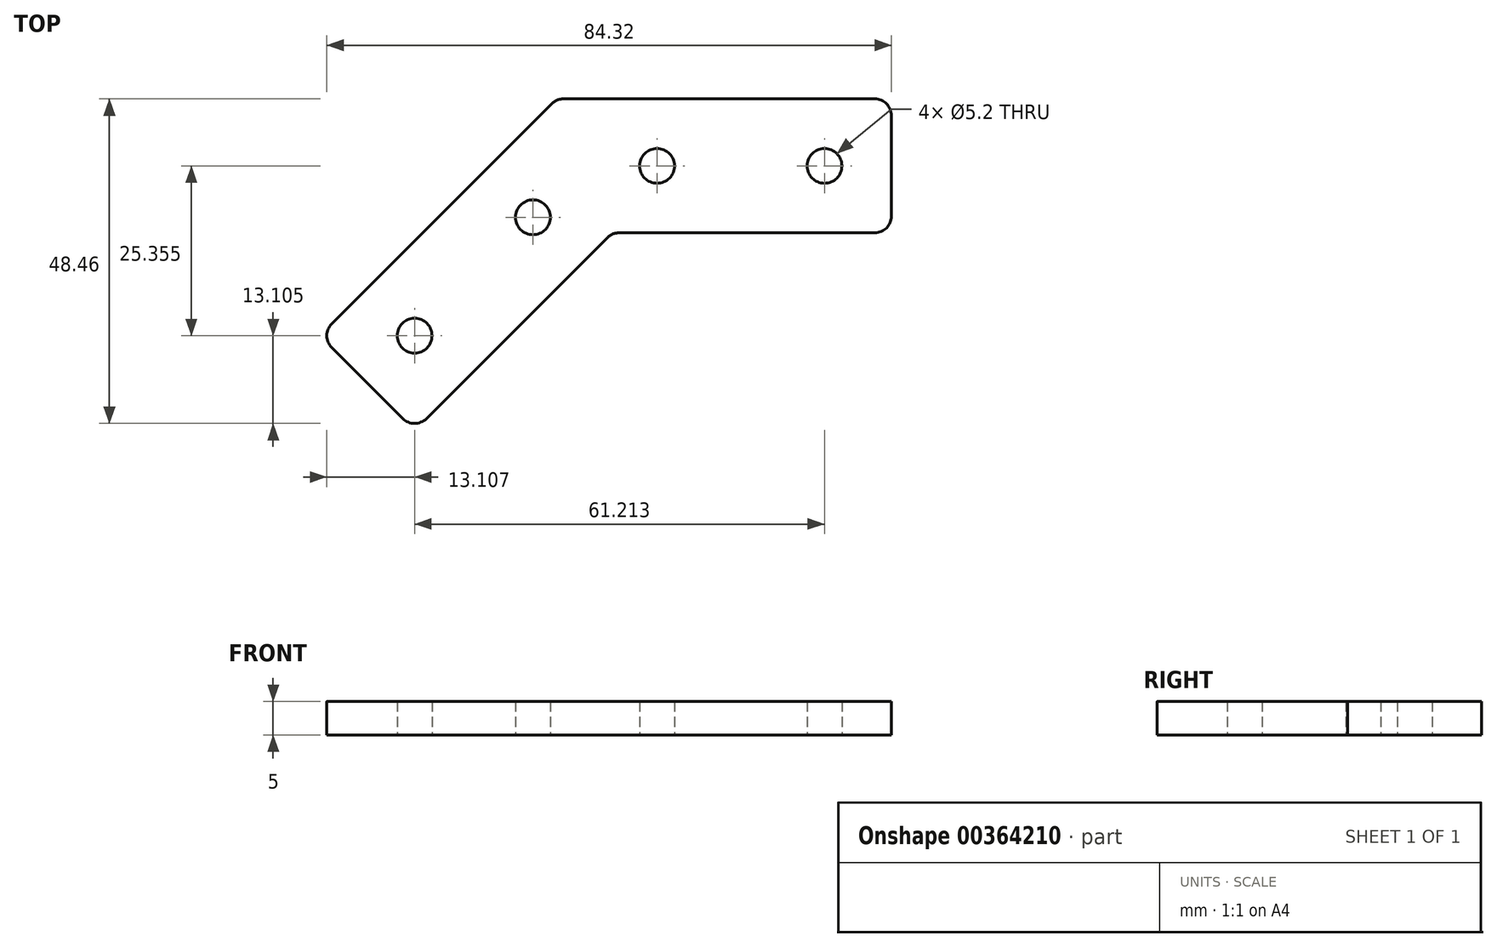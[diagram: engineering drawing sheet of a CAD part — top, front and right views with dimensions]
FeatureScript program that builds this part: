
annotation { "Feature Type Name" : "Feature", "Feature Type Description" : "" }
export const myFeature = defineFeature(function(context is Context, id is Id, definition is map)
    precondition{}
    {
        {
            var Q0;
            Q0=qCreatedBy(makeId("Top.planeOp"),FACE);
            var sketch = newSketch(context, id + "F0", { "sketchPlane" : qUnion([Q0])});
            skLineSegment(sketch, "E0", {"start": v(1.04, 0) * mm, "end": v(47.5, 0) * mm});
            skLineSegment(sketch, "E1", {"start": v(-0.73, -0.73) * mm, "end": v(-33.59, -33.59) * mm});
            skLineSegment(sketch, "E2", {"start": v(47.5, -20) * mm, "end": v(9.32, -20) * mm});
            skLineSegment(sketch, "E3", {"start": v(-19.45, -47.73) * mm, "end": v(7.55, -20.73) * mm});
            skPoint(sketch, "E4.orphan", {"position": v(0, -20) * mm});
            skLineSegment(sketch, "E5", {"start": v(-33.59, -37.12) * mm, "end": v(-22.98, -47.73) * mm});
            skLineSegment(sketch, "E6", {"start": v(50, -2.5) * mm, "end": v(50, -17.5) * mm});
            skPoint(sketch, "E7.orphan", {"position": v(31.21, -20) * mm});
            skPoint(sketch, "E8.visualSharp", {"position": v(50, 0) * mm});
            skArc(sketch, "E8.filletArc", {"start": v(50, -2.5) * mm, "mid": v(49.27, -0.73) * mm, "end": v(47.5, 0) * mm});
            skPoint(sketch, "E9.visualSharp", {"position": v(50, -20) * mm});
            skArc(sketch, "E9.filletArc", {"start": v(47.5, -20) * mm, "mid": v(49.27, -19.27) * mm, "end": v(50, -17.5) * mm});
            skPoint(sketch, "E10.visualSharp", {"position": v(0, 0) * mm});
            skArc(sketch, "E10.filletArc", {"start": v(1.04, 0) * mm, "mid": v(0.08, -0.2) * mm, "end": v(-0.73, -0.73) * mm});
            skPoint(sketch, "E11.visualSharp", {"position": v(-35.36, -35.36) * mm});
            skArc(sketch, "E11.filletArc", {"start": v(-33.59, -33.59) * mm, "mid": v(-34.32, -35.36) * mm, "end": v(-33.59, -37.12) * mm});
            skPoint(sketch, "E12.visualSharp", {"position": v(-21.21, -49.5) * mm});
            skArc(sketch, "E12.filletArc", {"start": v(-22.98, -47.73) * mm, "mid": v(-21.21, -48.46) * mm, "end": v(-19.45, -47.73) * mm});
            skPoint(sketch, "E13.visualSharp", {"position": v(8.28, -20) * mm});
            skArc(sketch, "E13.filletArc", {"start": v(9.32, -20) * mm, "mid": v(8.36, -20.2) * mm, "end": v(7.55, -20.73) * mm});
            skLineSegment(sketch, "E14", {"start": v(-28.28, -42.43) * mm, "end": v(8.9, -5.24) * mm, "construction": true});
            skLineSegment(sketch, "E15", {"start": v(50, -10) * mm, "end": v(-4.84, -10) * mm, "construction": true});
            skCircle(sketch, "E16", {"center": v(40, -10) * mm, "radius": 2.6 * mm});
            skCircle(sketch, "E17", {"center": v(15, -10) * mm, "radius": 2.6 * mm});
            skCircle(sketch, "E18", {"center": v(-21.21, -35.36) * mm, "radius": 2.6 * mm});
            skCircle(sketch, "E19", {"center": v(-3.54, -17.68) * mm, "radius": 2.6 * mm});
            skSolve(sketch);
        }
        {
            var Q0;
            Q0 = qSketchRegion(id + "F0", true);
            extrude(context, id + "F1", {"entities" : qUnion([Q0]), "depth" : 5 * mm});
        }
    });
